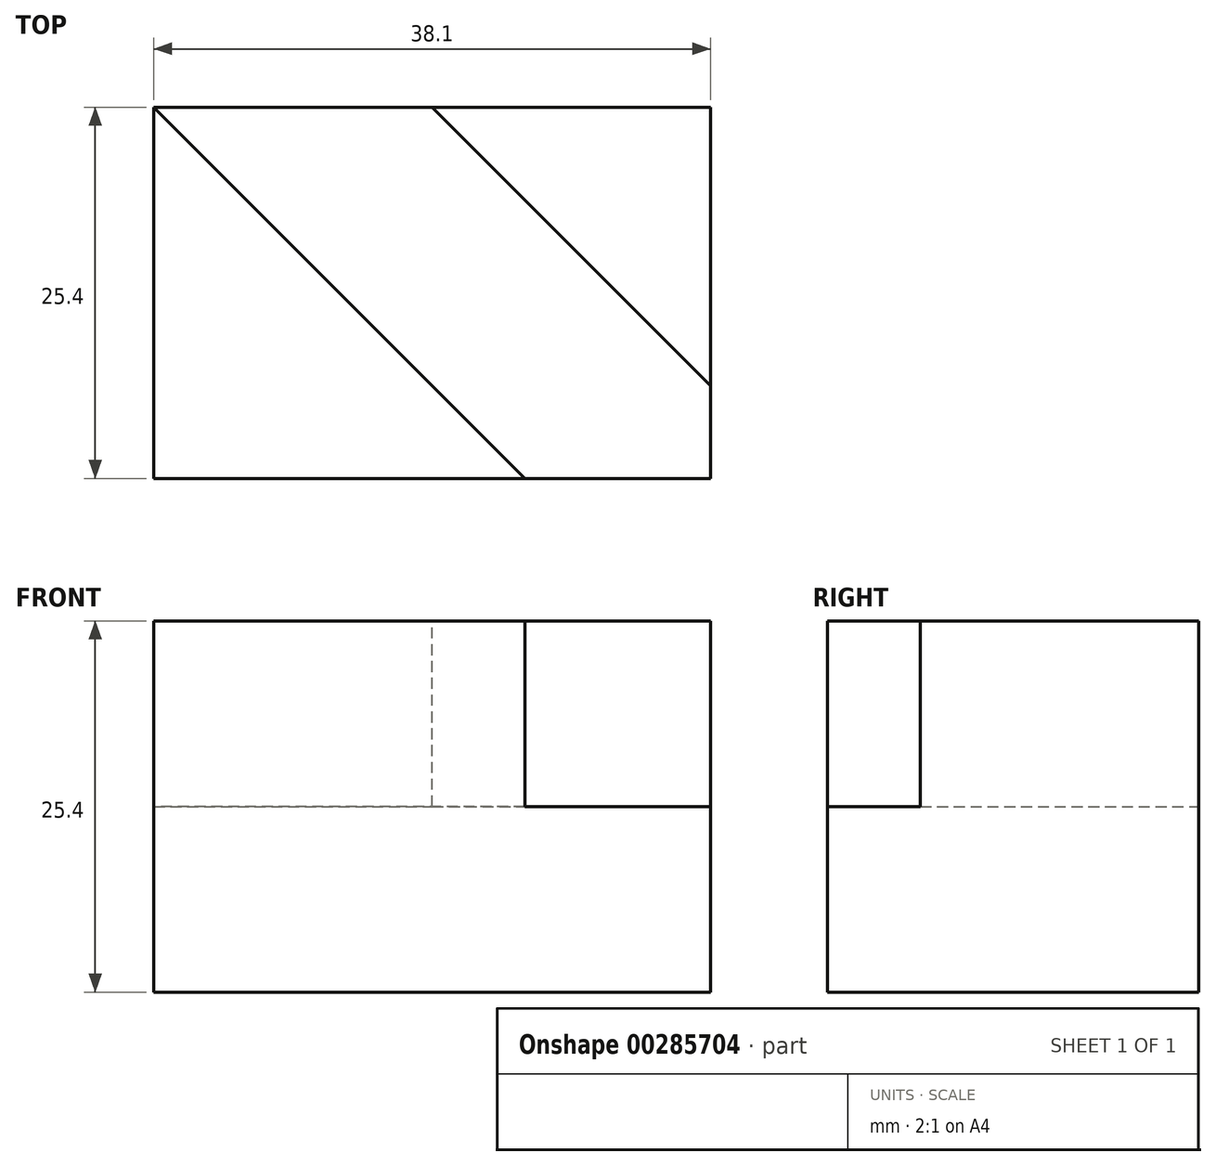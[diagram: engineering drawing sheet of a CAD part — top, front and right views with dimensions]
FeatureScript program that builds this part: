
annotation { "Feature Type Name" : "Feature", "Feature Type Description" : "" }
export const myFeature = defineFeature(function(context is Context, id is Id, definition is map)
    precondition{}
    {
        {
            var Q0;
            Q0=qCreatedBy(makeId("Top.planeOp"),FACE);
            var sketch = newSketch(context, id + "F0", { "sketchPlane" : qUnion([Q0])});
            skLineSegment(sketch, "E0.bottom", {"start": v(0, 0) * mm, "end": v(38.1, 0) * mm});
            skLineSegment(sketch, "E0.top", {"start": v(0, 25.4) * mm, "end": v(38.1, 25.4) * mm});
            skLineSegment(sketch, "E0.left", {"start": v(0, 0) * mm, "end": v(0, 25.4) * mm});
            skLineSegment(sketch, "E0.right", {"start": v(38.1, 0) * mm, "end": v(38.1, 25.4) * mm});
            skSolve(sketch);
        }
        {
            var Q0;
            Q0=makeQuery(id+"F0.imprint","IMPRINT",FACE,{"disambiguationData":[TD([[makeQuery(id+"F0.imprint","IMPRINT",EDGE,{"derivedFrom":sQuery(id+"F0.wireOp",EDGE,"E0.top")}),-1.0]])]});
            var Q1;
            Q1=makeQuery(id+"F0.imprint","IMPRINT",FACE,{"disambiguationData":[TD([[makeQuery(id+"F0.imprint","IMPRINT",EDGE,{"derivedFrom":sQuery(id+"F0.wireOp",EDGE,"E0.bottom")}),1.0]])]});
            var Q2;
            Q2=makeQuery(id+"F0.imprint","IMPRINT",FACE,{"disambiguationData":[TD([[makeQuery(id+"F0.imprint","IMPRINT",EDGE,{"derivedFrom":sQuery(id+"F0.wireOp",EDGE,"qf5AmnMn-kTej-9Keu-ltyN-TSdCXVBMY6nf")}),1.0]])]});
            extrude(context, id + "F1", {"entities" : qUnion([Q0, Q1, Q2]), "depth" : 25.4 * mm});
        }
        {
            var Q0;
            Q0=makeQuery(id+"F1.opExtrude","CAP_FACE",FACE,{"disambiguationData":[OSD([sQuery(id+"F0.wireOp",EDGE,"E0.bottom"),sQuery(id+"F0.wireOp",EDGE,"E0.top"),sQuery(id+"F0.wireOp",EDGE,"E0.left"),sQuery(id+"F0.wireOp",EDGE,"E0.right")])],"isStart":false});
            var sketch = newSketch(context, id + "F2", { "sketchPlane" : qUnion([Q0])});
            skLineSegment(sketch, "E1", {"start": v(38.1, 0) * mm, "end": v(38.1, 6.35) * mm});
            skLineSegment(sketch, "E2", {"start": v(38.1, 0) * mm, "end": v(25.4, 0) * mm});
            skLineSegment(sketch, "E3", {"start": v(25.4, 0) * mm, "end": v(0, 25.4) * mm});
            skLineSegment(sketch, "E4", {"start": v(0, 25.4) * mm, "end": v(19.05, 25.4) * mm});
            skLineSegment(sketch, "E5", {"start": v(19.05, 25.4) * mm, "end": v(38.1, 6.35) * mm});
            skSolve(sketch);
        }
        {
            var Q0;
            Q0 = qSketchRegion(id + "F2", true);
            extrude(context, id + "F3", {"entities" : qUnion([Q0]), "operationType" : NewBodyOperationType.REMOVE, "oppositeDirection" : true, "depth" : 12.7 * mm});
        }
    });
